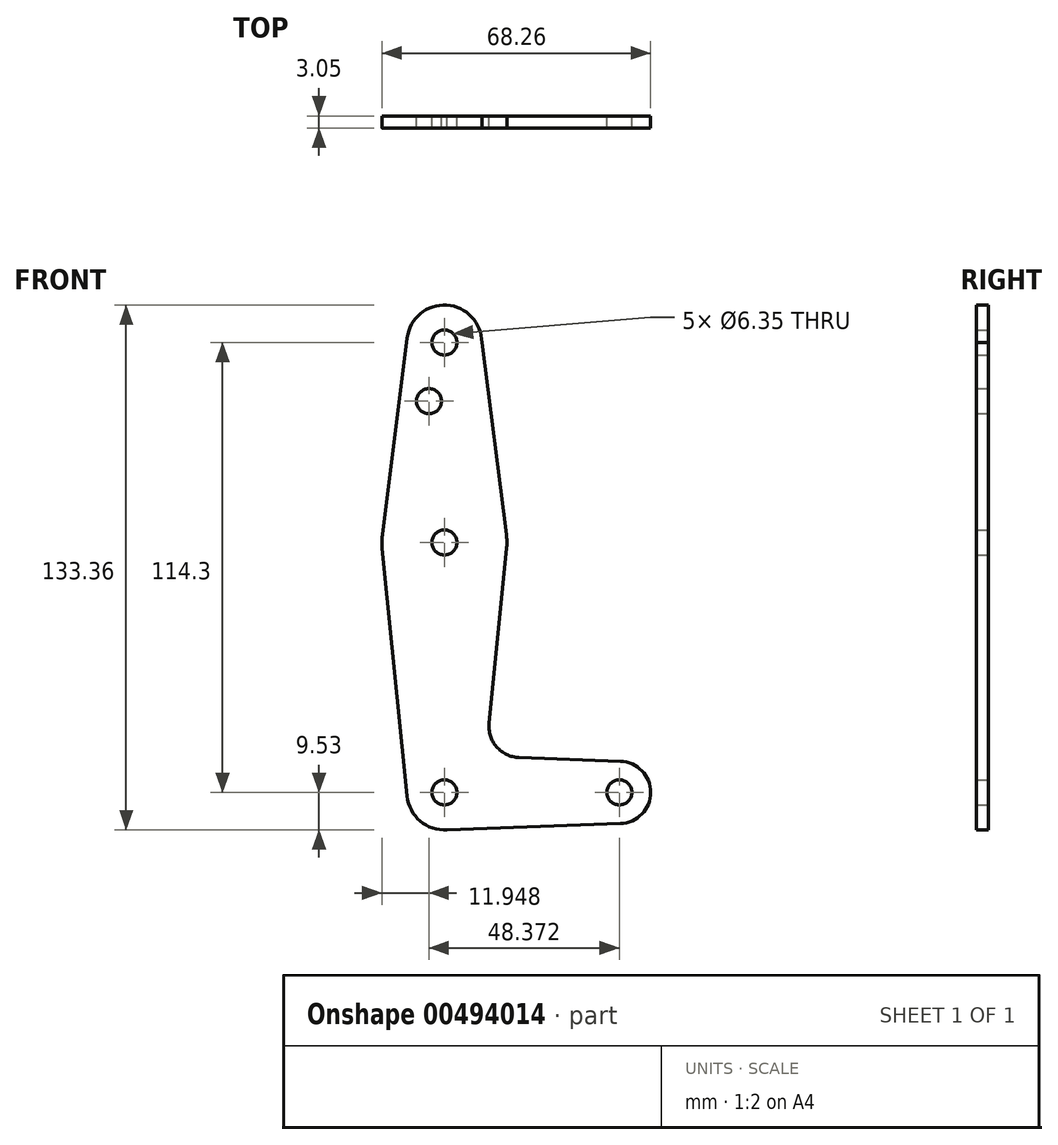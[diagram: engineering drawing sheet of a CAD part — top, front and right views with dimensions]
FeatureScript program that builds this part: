
annotation { "Feature Type Name" : "Feature", "Feature Type Description" : "" }
export const myFeature = defineFeature(function(context is Context, id is Id, definition is map)
    precondition{}
    {
        {
            var Q0;
            Q0=qCreatedBy(makeId("Front.planeOp"),FACE);
            var sketch = newSketch(context, id + "F0", { "sketchPlane" : qUnion([Q0])});
            skLineSegment(sketch, "E0", {"start": v(0, 0) * mm, "end": v(0, 114.3) * mm, "construction": true});
            skLineSegment(sketch, "E1", {"start": v(0, 0) * mm, "end": v(44.45, 0) * mm, "construction": true});
            skCircle(sketch, "E2", {"center": v(0, 114.3) * mm, "radius": 9.53 * mm});
            skCircle(sketch, "E3", {"center": v(0, 0) * mm, "radius": 9.53 * mm});
            skCircle(sketch, "E4", {"center": v(0, 63.5) * mm, "radius": 15.88 * mm});
            skCircle(sketch, "E5", {"center": v(44.45, 0) * mm, "radius": 7.94 * mm});
            skLineSegment(sketch, "E6", {"start": v(-9.45, 115.5) * mm, "end": v(-15.75, 65.48) * mm});
            skLineSegment(sketch, "E7", {"start": v(-9.48, -0.95) * mm, "end": v(-15.8, 61.91) * mm});
            skLineSegment(sketch, "E8", {"start": v(9.52, 114.3) * mm, "end": v(15.75, 65.48) * mm});
            skLineSegment(sketch, "E9", {"start": v(11.34, 17.6) * mm, "end": v(15.8, 61.91) * mm});
            skLineSegment(sketch, "E10", {"start": v(18.97, 8.85) * mm, "end": v(44.73, 7.93) * mm});
            skLineSegment(sketch, "E11", {"start": v(0, -9.53) * mm, "end": v(44.73, -7.93) * mm});
            skCircle(sketch, "E12", {"center": v(0, 114.3) * mm, "radius": 3.18 * mm});
            skCircle(sketch, "E13", {"center": v(0, 63.5) * mm, "radius": 3.18 * mm});
            skCircle(sketch, "E14", {"center": v(0, 0) * mm, "radius": 3.18 * mm});
            skCircle(sketch, "E15", {"center": v(44.45, 0) * mm, "radius": 3.18 * mm});
            skCircle(sketch, "E16", {"center": v(-3.92, 99.4) * mm, "radius": 3.18 * mm});
            skArc(sketch, "E17.filletArc", {"start": v(11.34, 17.6) * mm, "mid": v(13.26, 11.57) * mm, "end": v(18.97, 8.85) * mm});
            skSolve(sketch);
        }
        {
            var Q0;
            Q0 = qSketchRegion(id + "F0", true);
            extrude(context, id + "F1", {"entities" : qUnion([Q0]), "depth" : 3.05 * mm});
        }
    });
